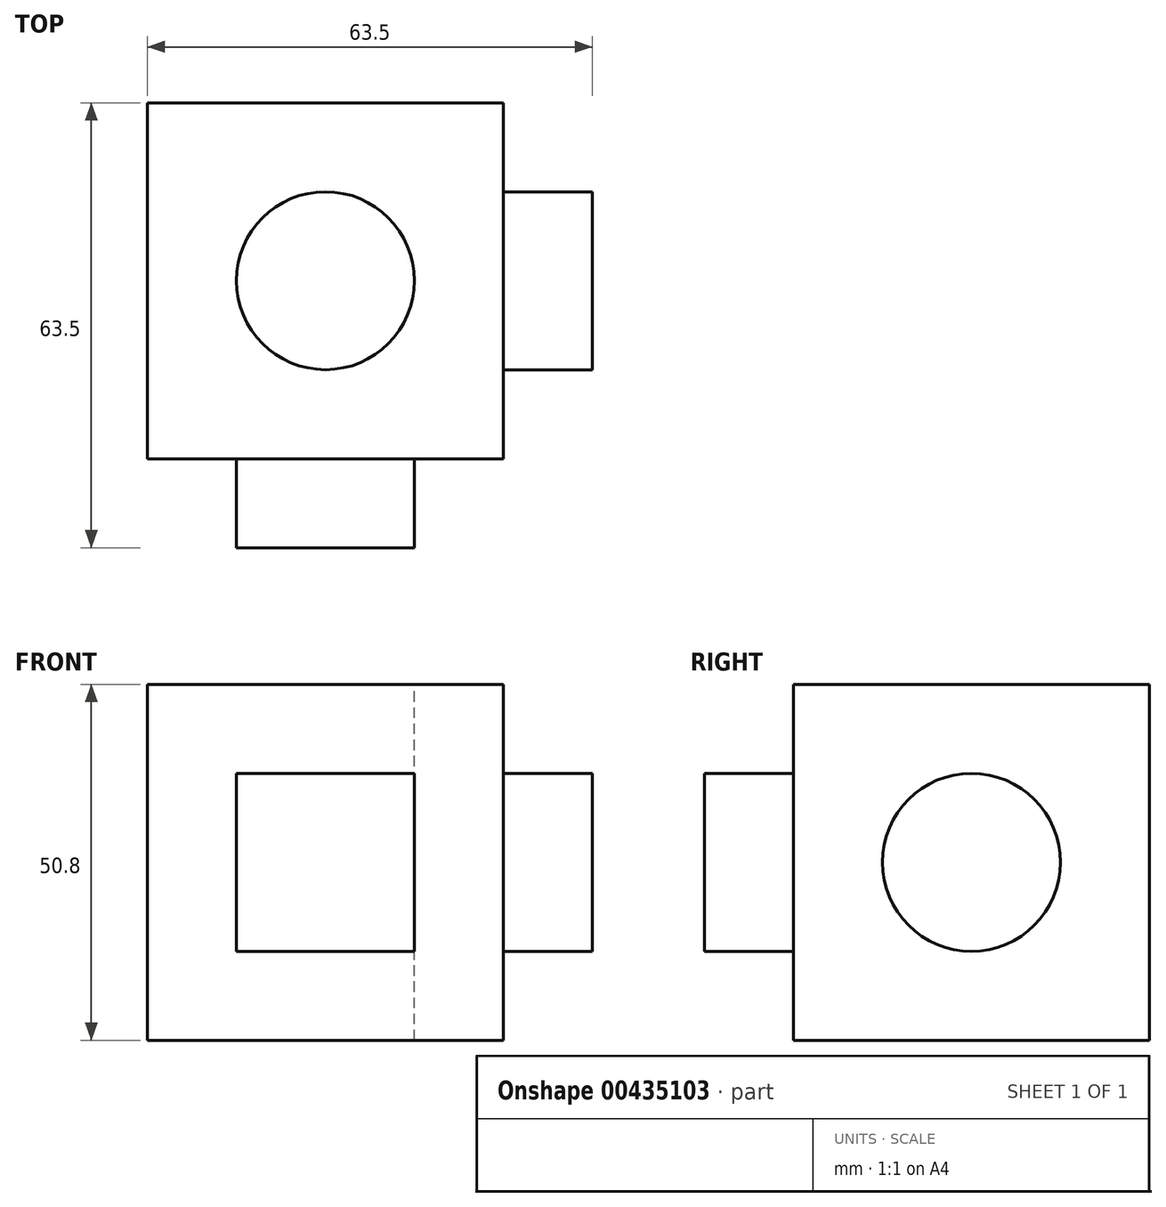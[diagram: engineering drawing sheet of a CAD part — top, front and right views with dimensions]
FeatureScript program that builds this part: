
annotation { "Feature Type Name" : "Feature", "Feature Type Description" : "" }
export const myFeature = defineFeature(function(context is Context, id is Id, definition is map)
    precondition{}
    {
        {
            var Q0;
            Q0=qCreatedBy(makeId("Front.planeOp"),FACE);
            var sketch = newSketch(context, id + "F0", { "sketchPlane" : qUnion([Q0])});
            skLineSegment(sketch, "E0.bottom", {"start": v(-47.55, -34.94) * mm, "end": v(3.25, -34.94) * mm});
            skLineSegment(sketch, "E0.top", {"start": v(-47.55, 15.86) * mm, "end": v(3.25, 15.86) * mm});
            skLineSegment(sketch, "E0.left", {"start": v(-47.55, -34.94) * mm, "end": v(-47.55, 15.86) * mm});
            skLineSegment(sketch, "E0.right", {"start": v(3.25, -34.94) * mm, "end": v(3.25, 15.86) * mm});
            skSolve(sketch);
        }
        {
            var Q0;
            Q0=makeQuery(id+"F0.imprint","IMPRINT",FACE,{"disambiguationData":[TD([[makeQuery(id+"F0.imprint","IMPRINT",EDGE,{"derivedFrom":sQuery(id+"F0.wireOp",EDGE,"E0.bottom")}),1.0]])]});
            extrude(context, id + "F1", {"entities" : qUnion([Q0]), "depth" : 50.8 * mm});
        }
        {
            var Q0;
            Q0=makeQuery(id+"F1.opExtrude","SWEPT_FACE",FACE,{"disambiguationData":[OSD([sQuery(id+"F0.wireOp",EDGE,"E0.top")])]});
            var sketch = newSketch(context, id + "F2", { "sketchPlane" : qUnion([Q0])});
            skCircle(sketch, "E1", {"center": v(-22.15, -25.4) * mm, "radius": 12.7 * mm});
            skSolve(sketch);
        }
        {
            var Q0;
            Q0=makeQuery(id+"F2.imprint","IMPRINT",FACE,{"disambiguationData":[TD([[makeQuery(id+"F2.imprint","IMPRINT",EDGE,{"derivedFrom":sQuery(id+"F2.wireOp",EDGE,"E1")}),1.0]])]});
            extrude(context, id + "F3", {"entities" : qUnion([Q0]), "operationType" : NewBodyOperationType.REMOVE, "oppositeDirection" : true, "depth" : 50.8 * mm});
        }
        {
            var Q0;
            Q0=makeQuery(id+"F1.opExtrude","CAP_FACE",FACE,{"disambiguationData":[OSD([sQuery(id+"F0.wireOp",EDGE,"E0.bottom"),sQuery(id+"F0.wireOp",EDGE,"E0.top"),sQuery(id+"F0.wireOp",EDGE,"E0.left"),sQuery(id+"F0.wireOp",EDGE,"E0.right")])],"isStart":false});
            var sketch = newSketch(context, id + "F4", { "sketchPlane" : qUnion([Q0])});
            skLineSegment(sketch, "E2.bottom", {"start": v(-34.85, -22.24) * mm, "end": v(-9.45, -22.24) * mm});
            skLineSegment(sketch, "E2.top", {"start": v(-34.85, 3.16) * mm, "end": v(-9.45, 3.16) * mm});
            skLineSegment(sketch, "E2.left", {"start": v(-34.85, -22.24) * mm, "end": v(-34.85, 3.16) * mm});
            skLineSegment(sketch, "E2.right", {"start": v(-9.45, -22.24) * mm, "end": v(-9.45, 3.16) * mm});
            skSolve(sketch);
        }
        {
            var Q0;
            Q0=makeQuery(id+"F4.imprint","IMPRINT",FACE,{"disambiguationData":[TD([[makeQuery(id+"F4.imprint","IMPRINT",EDGE,{"derivedFrom":sQuery(id+"F4.wireOp",EDGE,"E2.bottom")}),1.0]])]});
            extrude(context, id + "F5", {"entities" : qUnion([Q0]), "operationType" : NewBodyOperationType.ADD, "depth" : 12.7 * mm});
        }
        {
            var Q0;
            Q0=makeQuery(id+"F1.opExtrude","SWEPT_FACE",FACE,{"disambiguationData":[OSD([sQuery(id+"F0.wireOp",EDGE,"E0.right")])]});
            var sketch = newSketch(context, id + "F6", { "sketchPlane" : qUnion([Q0])});
            skCircle(sketch, "E3", {"center": v(-25.4, -9.54) * mm, "radius": 12.7 * mm});
            skSolve(sketch);
        }
        {
            var Q0;
            Q0=makeQuery(id+"F6.imprint","IMPRINT",FACE,{"disambiguationData":[TD([[makeQuery(id+"F6.imprint","IMPRINT",EDGE,{"derivedFrom":sQuery(id+"F6.wireOp",EDGE,"E3")}),1.0]])]});
            extrude(context, id + "F7", {"entities" : qUnion([Q0]), "operationType" : NewBodyOperationType.ADD, "depth" : 12.7 * mm});
        }
    });
